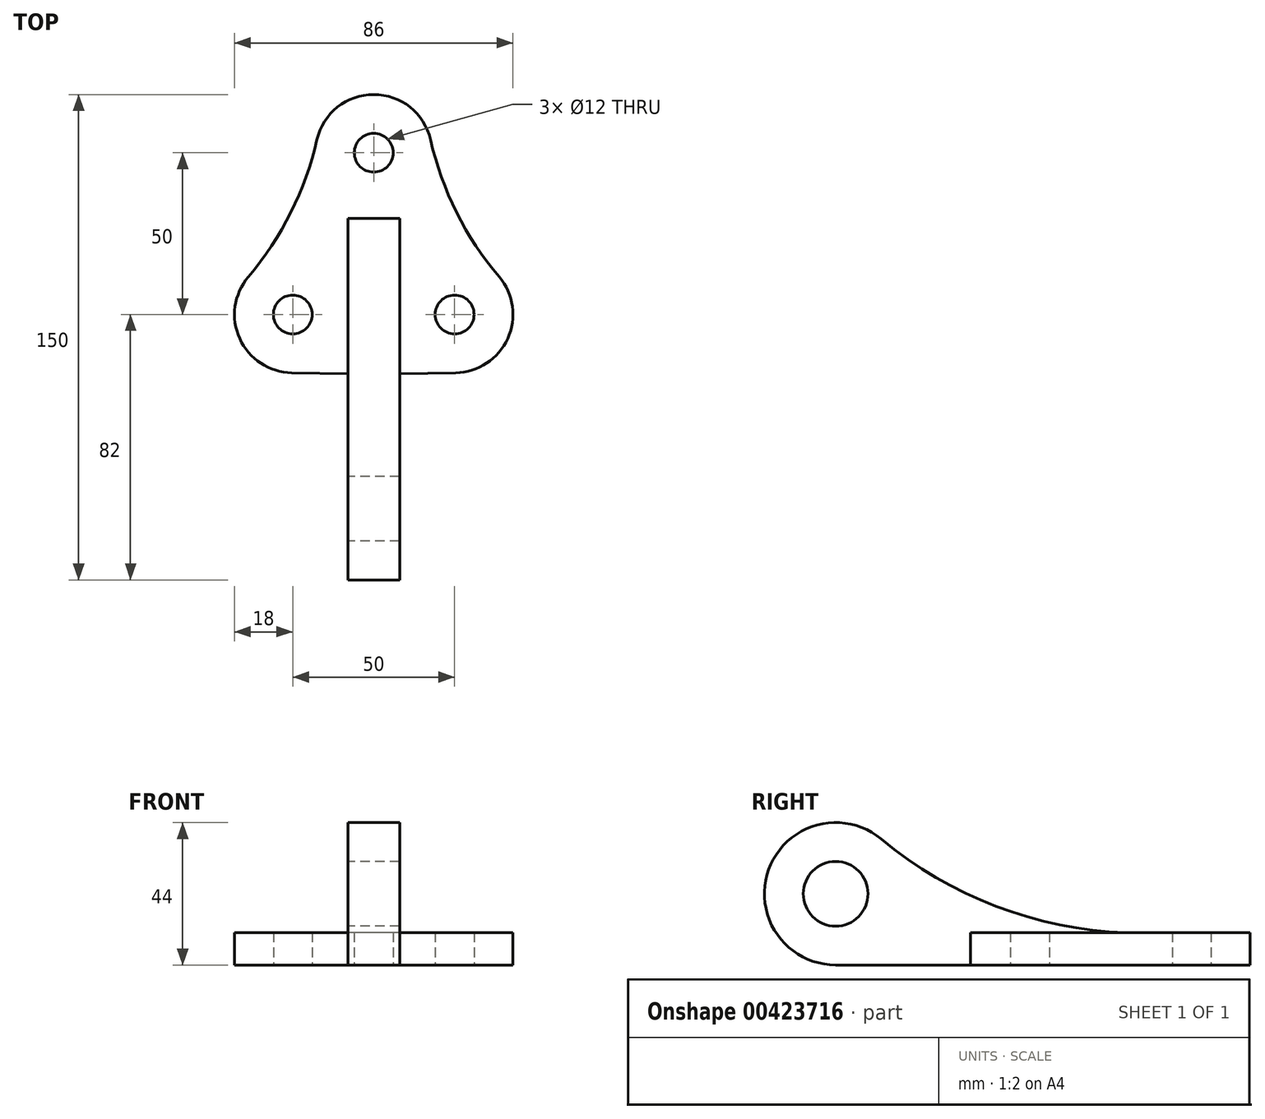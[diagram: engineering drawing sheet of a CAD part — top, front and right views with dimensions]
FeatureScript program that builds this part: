
annotation { "Feature Type Name" : "Feature", "Feature Type Description" : "" }
export const myFeature = defineFeature(function(context is Context, id is Id, definition is map)
    precondition{}
    {
        {
            var Q0;
            Q0=qCreatedBy(makeId("Top.planeOp"),FACE);
            var sketch = newSketch(context, id + "F0", { "sketchPlane" : qUnion([Q0])});
            skCircle(sketch, "E0", {"center": v(0, 50) * mm, "radius": 6 * mm});
            skCircle(sketch, "E1", {"center": v(25, 0) * mm, "radius": 6 * mm});
            skArc(sketch, "E2", {"start": v(17.55, 54) * mm, "mid": v(11.22, 64.07) * mm, "end": v(0, 68) * mm});
            skArc(sketch, "E3", {"start": v(25.32, -18) * mm, "mid": v(41.4, -7.42) * mm, "end": v(38.73, 11.63) * mm});
            skArc(sketch, "E4", {"start": v(17.55, 54) * mm, "mid": v(25.6, 31.55) * mm, "end": v(38.73, 11.63) * mm});
            skLineSegment(sketch, "E5", {"start": v(0, 75.93) * mm, "end": v(0, -50.72) * mm, "construction": true});
            skLineSegment(sketch, "E6", {"start": v(25.32, -18) * mm, "end": v(0, -18.45) * mm});
            skArc(sketch, "E7.MirrorCS", {"start": v(-17.55, 54) * mm, "mid": v(-11.22, 64.07) * mm, "end": v(0, 68) * mm});
            skArc(sketch, "E8.MirrorCS", {"start": v(-17.55, 54) * mm, "mid": v(-25.6, 31.55) * mm, "end": v(-38.73, 11.63) * mm});
            skArc(sketch, "E9.MirrorCS", {"start": v(-25.32, -18) * mm, "mid": v(-41.4, -7.42) * mm, "end": v(-38.73, 11.63) * mm});
            skLineSegment(sketch, "E10.MirrorCS", {"start": v(-25.32, -18) * mm, "end": v(0, -18.45) * mm});
            skCircle(sketch, "E11.MirrorC", {"center": v(-25, 0) * mm, "radius": 6 * mm});
            skSolve(sketch);
        }
        {
            var Q0;
            Q0=makeQuery(id+"F0.imprint","IMPRINT",FACE,{"disambiguationData":[TD([[makeQuery(id+"F0.imprint","IMPRINT",EDGE,{"derivedFrom":sQuery(id+"F0.wireOp",EDGE,"E0")}),-1.0]])]});
            extrude(context, id + "F1", {"entities" : qUnion([Q0]), "depth" : 10 * mm});
        }
        {
            var Q0;
            Q0=qCreatedBy(makeId("Right.planeOp"),FACE);
            var sketch = newSketch(context, id + "F2", { "sketchPlane" : qUnion([Q0])});
            skCircle(sketch, "E12", {"center": v(-60, 22) * mm, "radius": 10 * mm});
            skArc(sketch, "E13", {"start": v(-45.91, 38.9) * mm, "mid": v(-80.69, 29.5) * mm, "end": v(-60, 0) * mm});
            skArc(sketch, "E14", {"start": v(-45.91, 38.9) * mm, "mid": v(-10.52, 18.16) * mm, "end": v(29.68, 10) * mm});
            skLineSegment(sketch, "E15", {"start": v(29.68, 10) * mm, "end": v(42, 10) * mm});
            skLineSegment(sketch, "E16", {"start": v(42, 10) * mm, "end": v(42, 0) * mm});
            skPoint(sketch, "E17.orphan", {"position": v(54, 10) * mm});
            skLineSegment(sketch, "E18", {"start": v(-60, 0) * mm, "end": v(42, 0) * mm});
            skSolve(sketch);
        }
        {
            var Q0;
            Q0=makeQuery(id+"F2.imprint","IMPRINT",FACE,{"disambiguationData":[TD([[makeQuery(id+"F2.imprint","IMPRINT",EDGE,{"derivedFrom":sQuery(id+"F2.wireOp",EDGE,"E12")}),-1.0]])]});
            extrude(context, id + "F3", {"entities" : qUnion([Q0]), "operationType" : NewBodyOperationType.ADD, "endBound" : BoundingType.SYMMETRIC, "depth" : 16 * mm});
        }
    });
